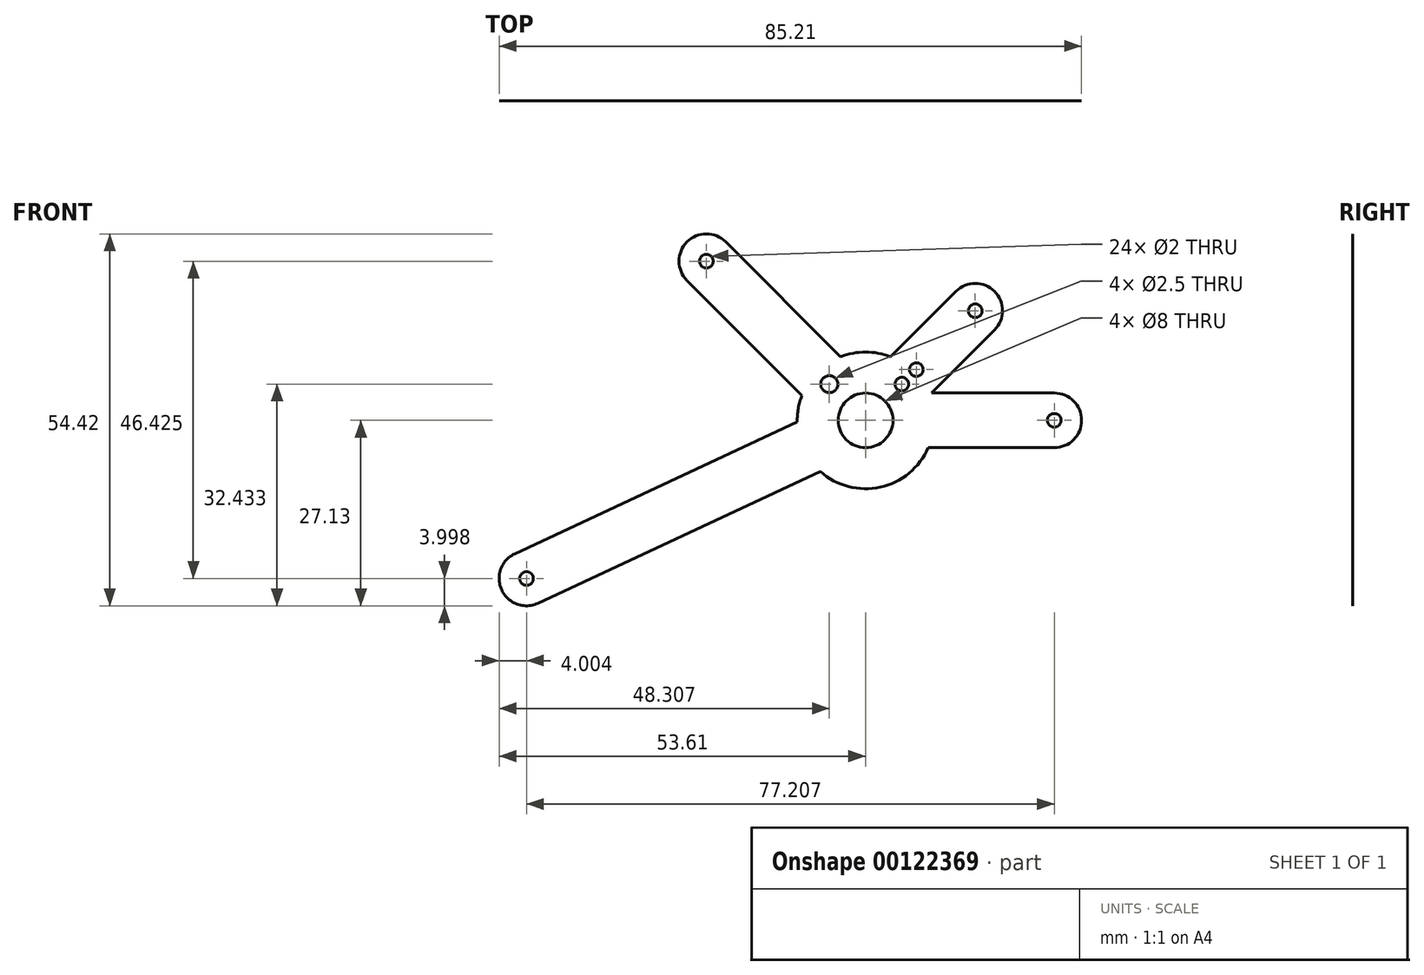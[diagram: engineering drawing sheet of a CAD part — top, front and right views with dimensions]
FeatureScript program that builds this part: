
annotation { "Feature Type Name" : "Feature", "Feature Type Description" : "" }
export const myFeature = defineFeature(function(context is Context, id is Id, definition is map)
    precondition{}
    {
        {
            var Q0;
            Q0=qCreatedBy(makeId("Front.planeOp"),FACE);
            var sketch = newSketch(context, id + "F0", { "sketchPlane" : qUnion([Q0])});
            skCircle(sketch, "E0", {"center": v(0, 0) * mm, "radius": 44.45 * mm});
            skArc(sketch, "E1", {"start": v(28.87, 28.12) * mm, "mid": v(28.87, 33.78) * mm, "end": v(23.21, 33.78) * mm});
            skArc(sketch, "E2", {"start": v(-10.46, 41.03) * mm, "mid": v(-16.12, 41.03) * mm, "end": v(-16.12, 35.37) * mm});
            skArc(sketch, "E3", {"start": v(-41.3, -4.6) * mm, "mid": v(-43.23, -9.91) * mm, "end": v(-37.92, -11.85) * mm});
            skArc(sketch, "E4", {"start": v(11.7, 11.28) * mm, "mid": v(10, 18.91) * mm, "end": v(8.3, 11.28) * mm});
            skLineSegment(sketch, "E5", {"start": v(-13.3, 38.2) * mm, "end": v(-12.59, 38.91) * mm});
            skLineSegment(sketch, "E6", {"start": v(-10.46, 41.03) * mm, "end": v(6.35, 24.22) * mm});
            skLineSegment(sketch, "E7", {"start": v(-13.3, 38.2) * mm, "end": v(-14, 37.5) * mm});
            skLineSegment(sketch, "E8", {"start": v(-16.12, 35.37) * mm, "end": v(0.7, 18.56) * mm});
            skLineSegment(sketch, "E9", {"start": v(-39.6, -8.22) * mm, "end": v(-40.03, -7.32) * mm});
            skLineSegment(sketch, "E10", {"start": v(-41.3, -4.6) * mm, "end": v(0, 14.66) * mm});
            skLineSegment(sketch, "E11", {"start": v(-39.6, -8.22) * mm, "end": v(-39.18, -9.13) * mm});
            skLineSegment(sketch, "E12", {"start": v(26.04, 30.95) * mm, "end": v(26.75, 30.24) * mm});
            skLineSegment(sketch, "E13", {"start": v(28.87, 28.12) * mm, "end": v(19.66, 18.91) * mm});
            skLineSegment(sketch, "E14", {"start": v(26.04, 30.95) * mm, "end": v(25.33, 31.66) * mm});
            skLineSegment(sketch, "E15", {"start": v(23.21, 33.78) * mm, "end": v(13.65, 24.22) * mm});
            skCircle(sketch, "E16", {"center": v(-13.3, 38.2) * mm, "radius": 1 * mm});
            skCircle(sketch, "E17", {"center": v(26.04, 30.95) * mm, "radius": 1 * mm});
            skCircle(sketch, "E18", {"center": v(-39.6, -8.22) * mm, "radius": 1 * mm});
            skLineSegment(sketch, "E19.trimOffspring", {"start": v(-16.12, 41.03) * mm, "end": v(-16.4, 41.31) * mm});
            skLineSegment(sketch, "E20.trimOffspring", {"start": v(-12.59, 37.5) * mm, "end": v(-14, 38.91) * mm});
            skLineSegment(sketch, "E21.trimOffspring", {"start": v(-38.7, -7.8) * mm, "end": v(-40.51, -8.64) * mm});
            skLineSegment(sketch, "E22.trimOffspring", {"start": v(25.33, 30.24) * mm, "end": v(26.75, 31.66) * mm});
            skArc(sketch, "E23.trimOffspring", {"start": v(7.17, 17.74) * mm, "mid": v(10, 10.91) * mm, "end": v(12.83, 17.74) * mm});
            skLineSegment(sketch, "E24.trimOffspring", {"start": v(-43.23, -9.91) * mm, "end": v(-43.32, -9.95) * mm});
            skLineSegment(sketch, "E25", {"start": v(10, 14.91) * mm, "end": v(26.04, 30.95) * mm});
            skLineSegment(sketch, "E26", {"start": v(-13.3, 38.2) * mm, "end": v(10, 14.91) * mm});
            skCircle(sketch, "E27", {"center": v(4.7, 20.21) * mm, "radius": 1.25 * mm});
            skCircle(sketch, "E28", {"center": v(15.3, 20.21) * mm, "radius": 1 * mm});
            skCircle(sketch, "E29", {"center": v(17.42, 22.33) * mm, "radius": 1 * mm});
            skLineSegment(sketch, "E30", {"start": v(10, 14.91) * mm, "end": v(14, 14.91) * mm});
            skArc(sketch, "E31", {"start": v(37.6, 10.91) * mm, "mid": v(41.6, 14.91) * mm, "end": v(37.6, 18.91) * mm});
            skLineSegment(sketch, "E32", {"start": v(37.6, 18.91) * mm, "end": v(19.66, 18.91) * mm});
            skLineSegment(sketch, "E33", {"start": v(-37.92, -11.85) * mm, "end": v(3.38, 7.41) * mm});
            skLineSegment(sketch, "E34", {"start": v(37.6, 10.91) * mm, "end": v(19.17, 10.91) * mm});
            skCircle(sketch, "E35", {"center": v(37.6, 14.91) * mm, "radius": 1 * mm});
            skLineSegment(sketch, "E36.trimOffspring", {"start": v(36.6, 14.91) * mm, "end": v(38.6, 14.91) * mm});
            skLineSegment(sketch, "E37.trimOffspring", {"start": v(41.6, 14.91) * mm, "end": v(41.87, 14.91) * mm});
            skArc(sketch, "E38.trimOffspring", {"start": v(0.7, 18.56) * mm, "mid": v(0.15, 16.65) * mm, "end": v(0, 14.66) * mm});
            skArc(sketch, "E39.trimOffspring", {"start": v(13.65, 24.22) * mm, "mid": v(10, 24.91) * mm, "end": v(6.35, 24.22) * mm});
            skArc(sketch, "E40.trimOffspring", {"start": v(3.38, 7.41) * mm, "mid": v(12.16, 5.15) * mm, "end": v(19.17, 10.91) * mm});
            skSolve(sketch);
        }
        {
            var Q0;
            {var subQ24=sQuery(id+"F0.wireOp",EDGE,"E4");Q0=makeQuery(id+"F0.imprint","IMPRINT",FACE,{"disambiguationData":[TD([[makeQuery(id+"F0.imprint","IMPRINT",EDGE,{"derivedFrom":subQ24}),-1.0]])]});}
            var Q1;
            {var subQ0=sQuery(id+"F0.wireOp",EDGE,"RFyr2Az2-A3VC-6oK4-Ao7S-vAKsB2PKfYEX");var subQ1=sQuery(id+"F0.wireOp",EDGE,"wJpxJIZD-nMre-bXtZ-ZupP-6sUj7CPpb7vH");var subQ2=makeQuery(id+"F0.imprint","INTERSECT",VERTEX,{"derivedFrom":[subQ1,subQ0]});Q1=makeQuery(id+"F0.imprint","IMPRINT",FACE,{"disambiguationData":[TD([[makeQuery(id+"F0.imprint","IMPRINT",EDGE,{"disambiguationData":[TD([[subQ2,1.0]])],"derivedFrom":subQ1}),-1.0]])]});}
            extrude(context, id + "F1", {"entities" : qUnion([Q0, Q1]), "depth" : 1 / 203.2 * mm});
        }
    });
